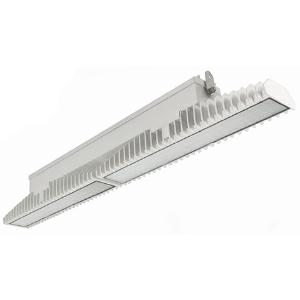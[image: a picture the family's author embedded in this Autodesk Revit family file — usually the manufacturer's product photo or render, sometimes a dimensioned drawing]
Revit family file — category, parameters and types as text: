
# Revit family: 3f_filippi_-_3f_lem_medio_3f_filippi_-_58896_a0812_-_3f_lem_1_1_led_100_cr_medio___vs_5cf7
name_source: partatom
category: Lighting Fixtures
units: mm (PartAtom-declared; Revit-internal decimal feet)

## family parameters
Cut with Voids When Loaded = No
Host = Face
Light Source = No
Part Type = Normal
Room Calculation Point = No
Round Connector Dimension = Use Diameter
Shared = No

## types (1)
- 3F Filippi - 3F LEM Medio (1 x LED, 13466 lm, 109 W, 4000 K)
    Apparent Load = 109 VA
    Approval mark = CE
    CIE Flux Codes = 77 92 98 100 100
    Color Rendering = 80
    Color Temperature = 4000 K
    Control Gear = Electronic ballast
    Default Elevation = 1800 mm
    Description = Industrial luminaire with high light output and high luminous efficiency designed with the most innovative technologies for environments with temperature up to 55°C.

ILLUMINOTECHNICAL
Luminous efficiency 100% (DLOR 98%, ULOR 2%).
Initial luminous flux of the luminaire 13466 lm.
Medium distribution with rectangular shape.
Installation Interdistance Transv.D = 0.87 x hu - Long.D = 0.87 x hu.
Tabular UGR (CIE 117 - 4H-8H; S=0.25H; 70/50/20): RUG 24.2 - 23.8.
Beam angle: 58° - 57°.
Luminous efficacy 124 lm/W.
Lifetime (L93/B10): 30000 h. (tq+25°C)
Lifetime (L90/B10): 50000 h. (tq+25°C)
Lifetime (L85/B10): 80000 h. (tq+25°C)
Lifetime (L80/B10): 100000 h. (tq+25°C)
Lifetime (L85/B10): 50000 h. (tq+55°C)
Sudden decreased luminous flux after 50000 hours: 0% (C0).
Photobiological safety in compliance with IEC/TR 62778: RG0 risk exempt, (IEC 62471).
In compliance with IEC/EN 62722-2-1 - IEC/EN 62717 standards.

SOURCE
2 Mid-Power linear LED modules 50W/840.
Energy efficiency class (UE 2019/2020 - UE 2019/2015): C.
CIE 13.3 Colour rendering index: CRI >80 (R9 <50%).
IES TM-30 Fidelity Index: Rf = 84 Rg = 95.
CCT nominal colour temperature 4000 K.
Colour initial tolerance (MacAdam): SDCM 3.

MECHANICAL
Passive modular heatsinks in die-casted aluminium, painted in white colour.
To optimize the thermal management of the LED module, the heatsinks are oversized and provided with self-cleaning of cooling fins.
Wiring body in aluminium and galvanised steel anchored solidly to the sinks and thermally separated.
3F Lens lenses with high luminous efficiency, transparent methacrylate (PMMA), fixed to the LED modules.
Fixing brackets in stainless steel.
Luminaire with limited surface temperature. - D - (EN 60598-2-24)
Dimensions: 1099x115 mm, height 154 mm. Weight 11.31 kg.
IP65 protection degree.
Mechanical strength to impacts IK06 (1 joule).
Glow-wire test resistance 650°C.

ELECTRICAL
Halogen Free electronic wiring 230V-50/60Hz, power factor 0.97, THD <25%, constant output current, class I, 1 driver.
Power of the luminaire 109 W.
ENEC - CE.
SAFE FLICKER: PstLM=<1 and SVM=<0.4 (IEC TR 61547-1 and IEC TR 63158), to ensure a more comfortable and safe light.
Luminaire compliant with EN 60598-2-22 for power supply from a centralised emergency system CPSS (Central Power Supply System), not incorporated in the luminaire - high risk areas excluded. The default power and flux are 100% in AC and 100% in DC.
Ambient temperature from -30°C to +55°C.
Temperature class T6 max 85°C.
Quick connection via M20 3P connector with 9-13 mm tightening range.
Power unit positioned on a separate compartment by the LED module to ensure optimum temperatures of cabling components, to be inspectable and maintainable.
Relative humidity UR: <85%.

INSTALLATION
Ceiling / Suspended / Wall.
All accessories dedicated to this product are available on the Catalog and on our website www.3F-Filippi.com.

ACCESSORIES
A0812 - Anti-glare microprismatic VS moulded glass, tempered, not flammable, with sealing gasket.
One required for each light module. The pack contains 10 pieces.

APPLICATIONS
In commercial environments, exhibition and industrial areas, stores, open areas.
Applications with high ambient temperature up to 55°C.
Environments in which it is necessary a total protection against falling fragments (eg environments with foodstuffs or machines with moving parts or with extreme temperature changes), use luminaires with polycarbonate lenses.

WARNING
Fixture not suitable for cold stores with an ambient temperature <0°C and/or relative humidity >85%.
Luminaire designed for disposal/recycling at end-of-life.
Replaceable (LED only) light source by a professional. Replaceable control gear by a professional.
    Height = 154 mm
    Lamp = 1 x LED
    Lamp Light Flux = 13466 lm
    Lamp Power = 109 W
    Lamp count = 1
    Length = 1099 mm
    Lifetime = 50000 h
    Luminous efficacy = 124 lm/W
    Manufacturer = 3F Filippi
    ModVariant = No
    Model = 3F Filippi - 58896+A0812 - 3F LEM 1+1 LED 100 CR MEDIO + VS
    Mounting Place = Ceiling
    Mounting Type = Pendant
    Number of Poles = 1
    OnlyDefault = Yes
    Power Factor = 1
    Product Name = 3F Filippi - 3F LEM Medio
    Product group = pendant luminaire
    ProductGroupID = 9
    Protection Class = Protection class I
    Protection Degree = IP 65
    RLX_Detail_Level = 1
    RLX_Emergency_Light_Flux = 0 lm
    RLX_Emergency_Type = 0
    RLX_Emergency_Type_DB = No
    RlxData = <blob elided: 91281 chars, md5=abed25c1>
    Socket = socket
    Standby Power = 0 W
    System Light Flux = 13466 lm
    System Power = 109 W
    Type Comments = Product without accessories
    Type Image = 3f_filippi_-_lem_11__a0812.jpg
    URL = http://relux.com
    VarID = ---
    Voltage = 0 V
    Weight = 0.00 kg
    Width = 115 mm

## geometry (parser evidence)
native form markers: Blend x4, Sweep x12
no freeform markers — native parametric forms only
